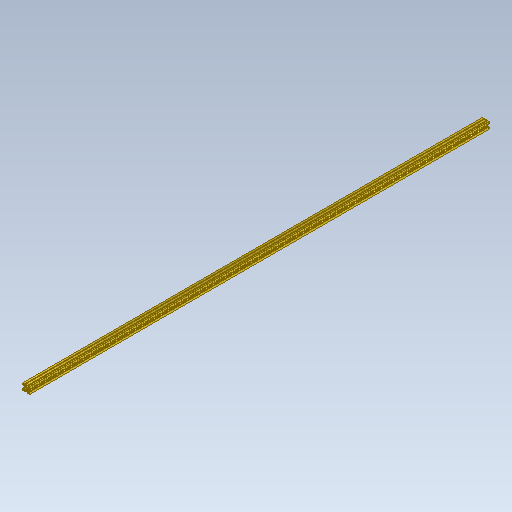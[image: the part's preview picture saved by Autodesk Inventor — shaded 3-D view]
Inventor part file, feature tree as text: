
AUTODESK INVENTOR PART (.ipt)
format: ipt  version: 2025.2 (Build 292293000, 293)  size: 347,648 bytes
history: native  units: mm
features: mirror x4, extrude x2, sketch x1
ambient origin geometry x8: Origin, YZ Plane, XZ Plane, XY Plane, X Axis, Y Axis, Z Axis, Center Point
bodies: Body1 (feature_tree)
feature tree (7):
  sketch  "Esboço1"  dims[d0=10.0mm d1=15.0mm d2=30.0mm d3=8.0mm d5=8.2mm d7=1.1mm d10=4.5mm d13=1.1mm d14=11.5mm d16=1.1mm d21=2.2mm d25=2.2mm d26=1.1mm d35=2000.0mm d36=0.0mm d37=2000.0mm d38=0.0mm d29=0.5mm d30=0.872665mm d31=0.5mm d32=0.872665mm d33=0.5mm d34=0.872665mm]
  extrude  "Extrusão5"  Depth=15.0mm
  mirror  "Espelhar11"
  mirror  "Espelhar12"
  mirror  "Espelhar13"
  extrude  "Extrusão6"  Depth=30.0mm
  mirror  "Espelhar14"
